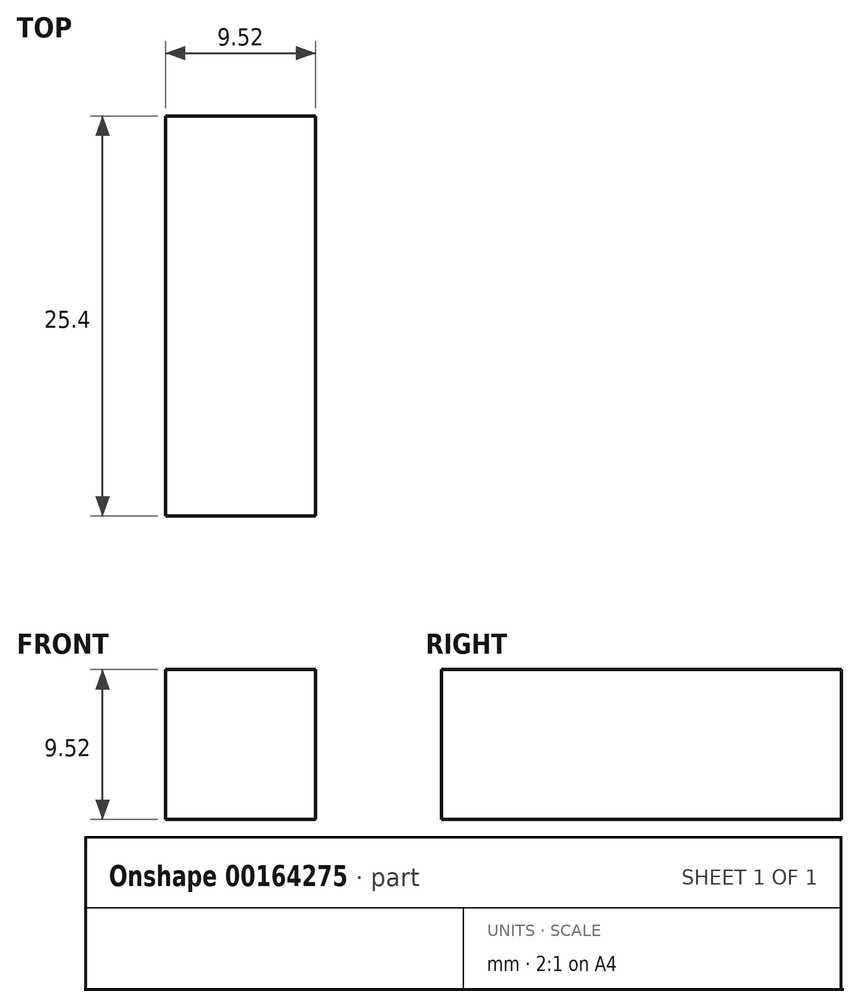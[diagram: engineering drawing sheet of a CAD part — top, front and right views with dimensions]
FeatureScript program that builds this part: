
annotation { "Feature Type Name" : "Feature", "Feature Type Description" : "" }
export const myFeature = defineFeature(function(context is Context, id is Id, definition is map)
    precondition{}
    {
        {
            var Q0;
            Q0=qCreatedBy(makeId("Front.planeOp"),FACE);
            var sketch = newSketch(context, id + "F0", { "sketchPlane" : qUnion([Q0])});
            skLineSegment(sketch, "E0.bottom", {"start": v(-4.76, 4.76) * mm, "end": v(4.76, 4.76) * mm});
            skLineSegment(sketch, "E0.top", {"start": v(-4.76, -4.76) * mm, "end": v(4.76, -4.76) * mm});
            skLineSegment(sketch, "E0.left", {"start": v(-4.76, 4.76) * mm, "end": v(-4.76, -4.76) * mm});
            skLineSegment(sketch, "E0.right", {"start": v(4.76, 4.76) * mm, "end": v(4.76, -4.76) * mm});
            skPoint(sketch, "E0.middle", {"position": v(0, 0) * mm});
            skCircle(sketch, "E1", {"center": v(0, 0) * mm, "radius": 4.76 * mm});
            skSolve(sketch);
        }
        {
            var Q0;
            Q0 = qSketchRegion(id + "F0", true);
            extrude(context, id + "F1", {"entities" : qUnion([Q0]), "depth" : 25.4 * mm});
        }
    });
